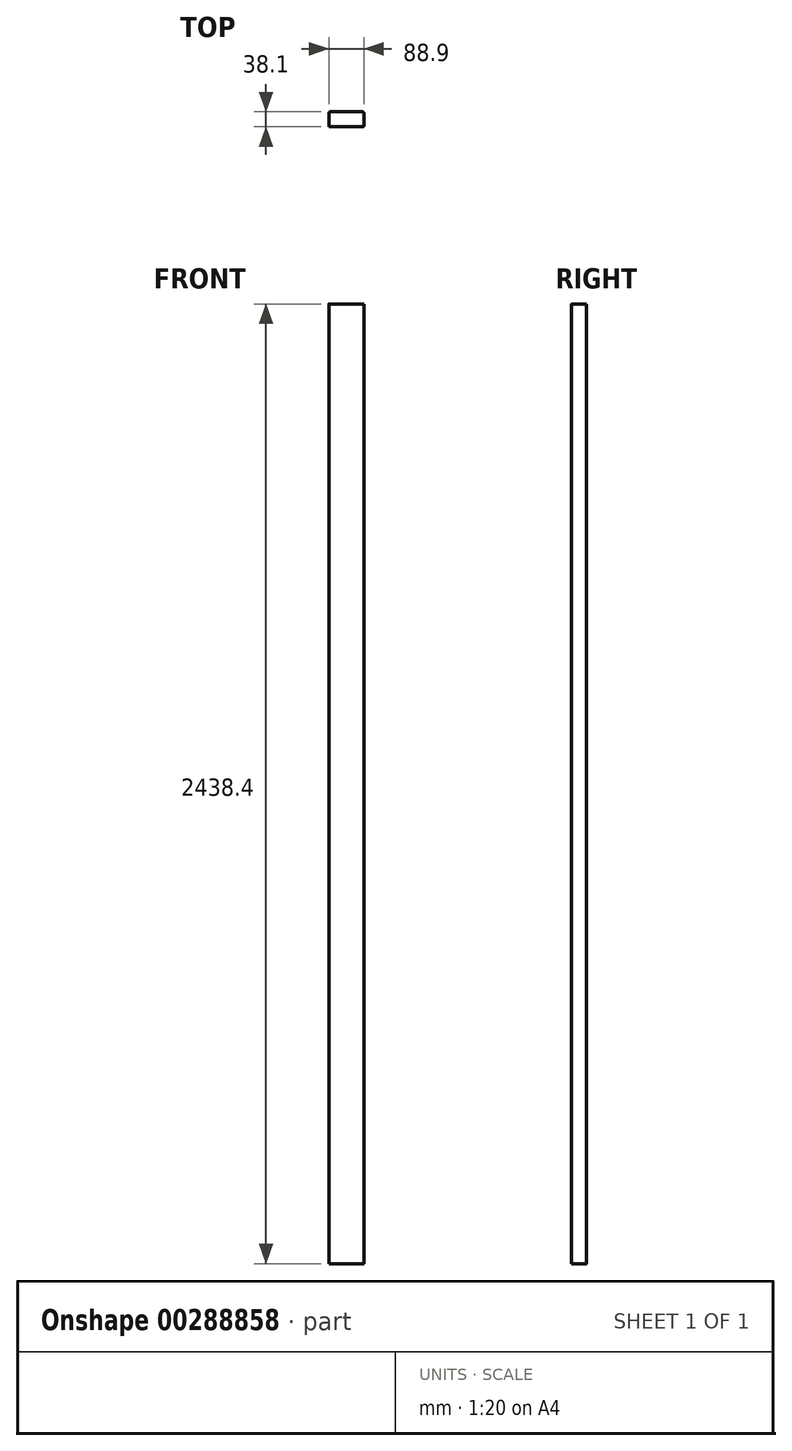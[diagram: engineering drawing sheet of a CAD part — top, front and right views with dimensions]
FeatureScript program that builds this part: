
annotation { "Feature Type Name" : "Feature", "Feature Type Description" : "" }
export const myFeature = defineFeature(function(context is Context, id is Id, definition is map)
    precondition{}
    {
        {
            var Q0;
            Q0=qCreatedBy(makeId("Top.planeOp"),FACE);
            var sketch = newSketch(context, id + "F0", { "sketchPlane" : qUnion([Q0])});
            skLineSegment(sketch, "E0.bottom", {"start": v(-144.18, 13.41) * mm, "end": v(-61.63, 13.41) * mm});
            skLineSegment(sketch, "E0.top", {"start": v(-144.18, -24.69) * mm, "end": v(-61.63, -24.69) * mm});
            skLineSegment(sketch, "E0.left", {"start": v(-147.35, 10.24) * mm, "end": v(-147.35, -21.51) * mm});
            skLineSegment(sketch, "E0.right", {"start": v(-58.45, 10.24) * mm, "end": v(-58.45, -21.51) * mm});
            skPoint(sketch, "E1.visualSharp", {"position": v(-147.35, 13.41) * mm});
            skArc(sketch, "E1.filletArc", {"start": v(-144.18, 13.41) * mm, "mid": v(-146.42, 12.48) * mm, "end": v(-147.35, 10.24) * mm});
            skPoint(sketch, "E2.visualSharp", {"position": v(-147.35, -24.69) * mm});
            skArc(sketch, "E2.filletArc", {"start": v(-147.35, -21.51) * mm, "mid": v(-146.42, -23.76) * mm, "end": v(-144.18, -24.69) * mm});
            skPoint(sketch, "E3.visualSharp", {"position": v(-58.45, -24.69) * mm});
            skArc(sketch, "E3.filletArc", {"start": v(-61.63, -24.69) * mm, "mid": v(-59.38, -23.76) * mm, "end": v(-58.45, -21.51) * mm});
            skPoint(sketch, "E4.visualSharp", {"position": v(-58.45, 13.41) * mm});
            skArc(sketch, "E4.filletArc", {"start": v(-58.45, 10.24) * mm, "mid": v(-59.38, 12.48) * mm, "end": v(-61.63, 13.41) * mm});
            skSolve(sketch);
        }
        {
            var Q0;
            Q0=makeQuery(id+"F0.imprint","IMPRINT",FACE,{"disambiguationData":[TD([[makeQuery(id+"F0.imprint","IMPRINT",EDGE,{"derivedFrom":sQuery(id+"F0.wireOp",EDGE,"E0.bottom")}),-1.0]])]});
            extrude(context, id + "F1", {"entities" : qUnion([Q0]), "depth" : 2438.4 * mm});
        }
        {
            var Q0;
            Q0=makeQuery(id+"F1.opExtrude","CAP_EDGE",EDGE,{"disambiguationData":[OSD([sQuery(id+"F0.wireOp",EDGE,"E0.bottom")])],"isStart":true});
            cPoint(context, id + "F2", {"entities" : qUnion([Q0]), "parameter" : 0.5});
        }
        {
            var Q0;
            Q0=makeQuery(id+"F1.opExtrude","SWEPT_BODY",BODY,{"disambiguationData":[OSD([sQuery(id+"F0.wireOp",EDGE,"E0.bottom"),sQuery(id+"F0.wireOp",EDGE,"E0.top"),sQuery(id+"F0.wireOp",EDGE,"E0.left"),sQuery(id+"F0.wireOp",EDGE,"E0.right"),sQuery(id+"F0.wireOp",EDGE,"E1.filletArc"),sQuery(id+"F0.wireOp",EDGE,"E2.filletArc"),sQuery(id+"F0.wireOp",EDGE,"E3.filletArc"),sQuery(id+"F0.wireOp",EDGE,"E4.filletArc")])]});
            var Q1;
            Q1 = qCreatedBy(id + "F2" ,VERTEX);
            var Q2;
            Q2=qCreatedBy(makeId("Origin.pointOp"),VERTEX);
            transform(context, id + "F3", {"entities" : qUnion([Q0]), "transformType" : TransformType.TRANSLATION_ENTITY, "oppositeDirectionEntity" : false, "transformLine" : qUnion([Q1, Q2]), "makeCopy" : false});
        }
    });
